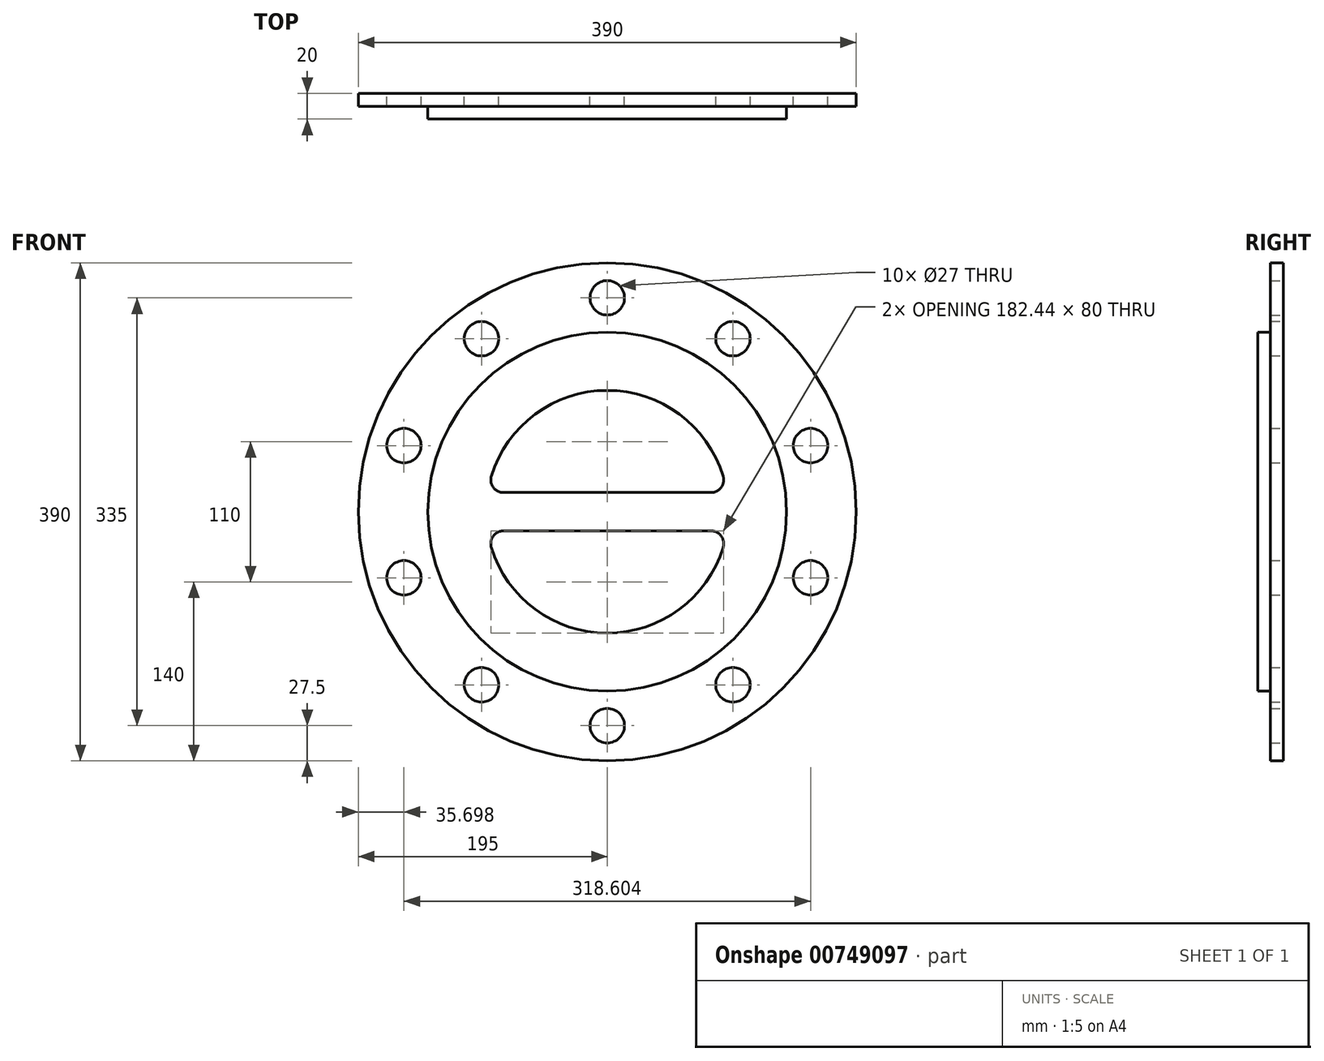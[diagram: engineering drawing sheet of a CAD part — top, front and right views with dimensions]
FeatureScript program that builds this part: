
annotation { "Feature Type Name" : "Feature", "Feature Type Description" : "" }
export const myFeature = defineFeature(function(context is Context, id is Id, definition is map)
    precondition{}
    {
        {
            var Q0;
            Q0=qCreatedBy(makeId("Front.planeOp"),FACE);
            var sketch = newSketch(context, id + "F0", { "sketchPlane" : qUnion([Q0])});
            skCircle(sketch, "E0", {"center": v(0, 0) * mm, "radius": 195 * mm});
            skCircle(sketch, "E1", {"center": v(0, 167.5) * mm, "radius": 13.5 * mm});
            skCircle(sketch, "E2.1.0", {"center": v(-98.45, 135.51) * mm, "radius": 13.5 * mm});
            skCircle(sketch, "E2.2.0", {"center": v(-159.3, 51.76) * mm, "radius": 13.5 * mm});
            skCircle(sketch, "E2.3.0", {"center": v(-159.3, -51.76) * mm, "radius": 13.5 * mm});
            skCircle(sketch, "E2.4.0", {"center": v(-98.45, -135.51) * mm, "radius": 13.5 * mm});
            skCircle(sketch, "E2.5.0", {"center": v(0, -167.5) * mm, "radius": 13.5 * mm});
            skCircle(sketch, "E2.6.0", {"center": v(98.45, -135.51) * mm, "radius": 13.5 * mm});
            skCircle(sketch, "E2.7.0", {"center": v(159.3, -51.76) * mm, "radius": 13.5 * mm});
            skCircle(sketch, "E2.8.0", {"center": v(159.3, 51.76) * mm, "radius": 13.5 * mm});
            skCircle(sketch, "E2.9.0", {"center": v(98.45, 135.51) * mm, "radius": 13.5 * mm});
            skCircle(sketch, "E3", {"center": v(0, 0) * mm, "radius": 140.5 * mm});
            skSolve(sketch);
        }
        {
            var Q0;
            Q0=makeQuery(id+"F0.imprint","IMPRINT",FACE,{"disambiguationData":[TD([[makeQuery(id+"F0.imprint","IMPRINT",EDGE,{"derivedFrom":sQuery(id+"F0.wireOp",EDGE,"E3")}),1.0]])]});
            extrude(context, id + "F1", {"entities" : qUnion([Q0]), "depth" : 20 * mm, "offsetDistance" : 25 * mm});
        }
        {
            var Q0;
            Q0=qSketchRegion(id+"F0",true);
            extrude(context, id + "F2", {"entities" : qUnion([Q0]), "operationType" : NewBodyOperationType.ADD, "depth" : 10 * mm, "offsetDistance" : 25 * mm});
        }
        {
            var Q0;
            Q0=makeQuery(id+"F1.opExtrude","CAP_FACE",FACE,{"disambiguationData":[OSD([sQuery(id+"F0.wireOp",EDGE,"E3")])],"isStart":false});
            var sketch = newSketch(context, id + "F3", { "sketchPlane" : qUnion([Q0])});
            skArc(sketch, "E4", {"start": v(90.8, 27.94) * mm, "mid": v(0, 95) * mm, "end": v(-90.8, 27.94) * mm});
            skLineSegment(sketch, "E5", {"start": v(-81.24, 15) * mm, "end": v(81.24, 15) * mm});
            skLineSegment(sketch, "E6", {"start": v(-81.24, -15) * mm, "end": v(81.24, -15) * mm});
            skArc(sketch, "E7.trimOffspring", {"start": v(-90.8, -27.94) * mm, "mid": v(0, -95) * mm, "end": v(90.8, -27.94) * mm});
            skPoint(sketch, "E8.visualSharp", {"position": v(-93.8, 15) * mm});
            skArc(sketch, "E8.filletArc", {"start": v(-90.8, 27.94) * mm, "mid": v(-89.28, 19.06) * mm, "end": v(-81.24, 15) * mm});
            skPoint(sketch, "E9.visualSharp", {"position": v(93.8, 15) * mm});
            skArc(sketch, "E9.filletArc", {"start": v(81.24, 15) * mm, "mid": v(89.28, 19.06) * mm, "end": v(90.8, 27.94) * mm});
            skPoint(sketch, "E10.visualSharp", {"position": v(93.8, -15) * mm});
            skArc(sketch, "E10.filletArc", {"start": v(90.8, -27.94) * mm, "mid": v(89.28, -19.06) * mm, "end": v(81.24, -15) * mm});
            skPoint(sketch, "E11.visualSharp", {"position": v(-93.8, -15) * mm});
            skArc(sketch, "E11.filletArc", {"start": v(-81.24, -15) * mm, "mid": v(-89.28, -19.06) * mm, "end": v(-90.8, -27.94) * mm});
            skSolve(sketch);
        }
        {
            var Q0;
            Q0=makeQuery(id+"F3.imprint","IMPRINT",FACE,{"disambiguationData":[TD([[makeQuery(id+"F3.imprint","IMPRINT",EDGE,{"derivedFrom":sQuery(id+"F3.wireOp",EDGE,"E4")}),1.0]])]});
            var Q1;
            Q1=makeQuery(id+"F3.imprint","IMPRINT",FACE,{"disambiguationData":[TD([[makeQuery(id+"F3.imprint","IMPRINT",EDGE,{"derivedFrom":sQuery(id+"F3.wireOp",EDGE,"E6")}),-1.0]])]});
            extrude(context, id + "F4", {"entities" : qUnion([Q0, Q1]), "operationType" : NewBodyOperationType.REMOVE, "oppositeDirection" : true, "depth" : 25 * mm, "offsetDistance" : 25 * mm});
        }
    });
